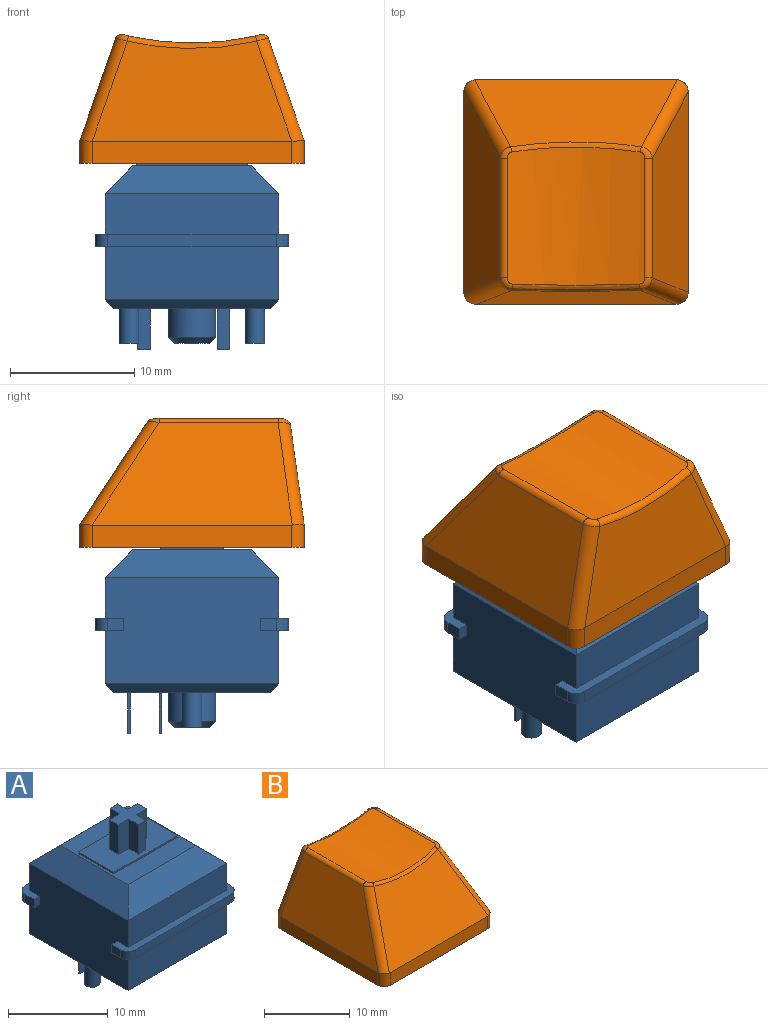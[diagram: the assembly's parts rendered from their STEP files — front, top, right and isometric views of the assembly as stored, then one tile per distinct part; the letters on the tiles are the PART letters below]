
ASSEMBLY  parts=2 mates=1
PART A: 69 faces, bbox 15.6x15.6x18.6 mm
  f0: plane 15.6x2.3mm, normal (0,0,-1), area 14.4mm2, adj f2,f3,f28,f30,f35,f60,f62,f63
  f1: plane 15.6x2.3mm, normal (0,0,-1), area 14.4mm2, adj f28,f30,f33,f34,f36,f59,f61,f64
  f2: plane 1.3x1mm, normal (1,0,0), area 1.3mm2, adj f0,f32,f62,f66
  f3: plane 1.3x1mm, normal (-1,0,0), area 1.3mm2, adj f0,f32,f63,f68
  f4: plane 15.6x2.3mm, normal (0,0,1), area 14.4mm2, adj f28,f30,f31,f33,f34,f36,f61,f64
  f5: plane 14x2.2mm, normal (-0.71,0,0.71), area 36.7mm2, adj f6,f7,f26,f30
  f6: plane 14x2.2mm, normal (0,-0.71,0.71), area 36.7mm2, adj f5,f7,f27,f31
  f7: plane 9.6x9.6mm, normal (0,0,1), area 47.2mm2, adj f5,f6,f8,f9,f10,f11,f26,f27
  f8: plane 5x0.2mm, normal (1,0,0), area 1mm2, adj f7,f9,f11,f12
  f9: plane 9x0.2mm, normal (0,1,0), area 1.8mm2, adj f7,f8,f10,f12
  f10: plane 5x0.2mm, normal (-1,0,0), area 1mm2, adj f7,f9,f11,f12
  f11: plane 9x0.2mm, normal (0,-1,0), area 1.8mm2, adj f7,f8,f10,f12
  f12: plane 9x5mm, normal (0,0,1), area 36.9mm2, adj f8,f9,f10,f11,f13,f14,f15,f16
  f13: plane 3.6x1.35mm, normal (1,0,0), area 4.9mm2, adj f12,f14,f24,f25
  f14: plane 3.6x1.08mm, normal (0,1,0), area 3.9mm2, adj f12,f13,f15,f25
  f15: plane 3.6x1.35mm, normal (-1,0,0), area 4.9mm2, adj f12,f14,f16,f25
  f16: plane 3.6x1.46mm, normal (0,1,0), area 5.3mm2, adj f12,f15,f17,f25
  f17: plane 3.6x1.3mm, normal (-1,0,0), area 4.7mm2, adj f12,f16,f18,f25
  f18: plane 3.6x1.46mm, normal (0,-1,0), area 5.3mm2, adj f12,f17,f19,f25
  f19: plane 3.6x1.35mm, normal (-1,0,0), area 4.9mm2, adj f12,f18,f20,f25
  f20: plane 3.6x1.08mm, normal (0,-1,0), area 3.9mm2, adj f12,f19,f21,f25
  f21: plane 3.6x1.35mm, normal (1,0,0), area 4.9mm2, adj f12,f20,f22,f25
  f22: plane 3.6x1.46mm, normal (0,-1,0), area 5.3mm2, adj f12,f21,f23,f25
  f23: plane 3.6x1.3mm, normal (1,0,0), area 4.7mm2, adj f12,f22,f24,f25
  f24: plane 3.6x1.46mm, normal (0,1,0), area 5.3mm2, adj f12,f13,f23,f25
  f25: plane 4x4mm, normal (0,0,1), area 8.1mm2, adj f13,f14,f15,f16,f17,f18,f19,f20
  f26: plane 14x2.2mm, normal (0,0.71,0.71), area 36.7mm2, adj f5,f7,f27,f29
  f27: plane 14x2.2mm, normal (0.71,0,0.71), area 36.7mm2, adj f6,f7,f26,f28
  f28: plane 14x8.6mm, normal (1,0,0), area 117.4mm2, adj f0,f1,f4,f27,f29,f31,f32,f55
  f29: plane 14x3.3mm, normal (0,1,0), area 46.2mm2, adj f26,f28,f30,f32
  f30: plane 14x8.6mm, normal (-1,0,0), area 117.4mm2, adj f0,f1,f4,f5,f29,f31,f32,f57
  f31: plane 14x3.3mm, normal (0,-1,0), area 46.2mm2, adj f4,f6,f28,f30
  f32: plane 15.6x2.3mm, normal (0,0,1), area 14.4mm2, adj f2,f3,f28,f29,f30,f35,f62,f63
  f33: plane 13.6x1mm, normal (0,-1,0), area 13.6mm2, adj f1,f4,f61,f64
  f34: plane 1.3x1mm, normal (1,0,0), area 1.3mm2, adj f1,f4,f61,f65
  f35: plane 13.6x1mm, normal (0,1,0), area 13.6mm2, adj f0,f32,f62,f63
  f36: plane 1.3x1mm, normal (-1,0,0), area 1.3mm2, adj f1,f4,f64,f67
  f37: plane 2.85x2.85mm, normal (0,0,-1), area 6.4mm2, adj f38
  f38: cone r=1.43mm half-angle=45deg, axis (0,0,1), area 7.4mm2, adj f37,f43
  f39: plane 1x0.2mm, normal (0,0,-1), area 0.2mm2, adj f44,f45,f46,f47
  f40: plane 1x0.2mm, normal (0,0,-1), area 0.2mm2, adj f48,f49,f50,f51
  f41: plane 1.6x1.6mm, normal (0,0,-1), area 2mm2, adj f52
  f42: plane 1.6x1.6mm, normal (0,0,-1), area 2mm2, adj f53
  f43: cylinder r=1.93mm len=3.85mm, axis (0,0,1), area 27.8mm2, adj f38,f54
  f44: plane 3.3x0.2mm, normal (-1,0,0), area 0.7mm2, adj f39,f45,f47,f54
  f45: plane 3.3x1mm, normal (0,1,0), area 3.3mm2, adj f39,f44,f46,f54
  f46: plane 3.3x0.2mm, normal (1,0,0), area 0.7mm2, adj f39,f45,f47,f54
  f47: plane 3.3x1mm, normal (0,-1,0), area 3.3mm2, adj f39,f44,f46,f54
  f48: plane 3.3x0.2mm, normal (-1,0,0), area 0.7mm2, adj f40,f49,f51,f54
  f49: plane 3.3x1mm, normal (0,1,0), area 3.3mm2, adj f40,f48,f50,f54
  f50: plane 3.3x0.2mm, normal (1,0,0), area 0.7mm2, adj f40,f49,f51,f54
  f51: plane 3.3x1mm, normal (0,-1,0), area 3.3mm2, adj f40,f48,f50,f54
  f52: cylinder r=0.8mm len=2.8mm, axis (0,0,1), area 14.1mm2, adj f41,f54
  f53: cylinder r=0.8mm len=2.8mm, axis (0,0,1), area 14.1mm2, adj f42,f54
  f54: plane 12.6x12.6mm, normal (0,0,-1), area 142.7mm2, adj f43,f44,f45,f46,f47,f48,f49,f50
  f55: plane 14x0.7mm, normal (0.71,0,-0.71), area 13.2mm2, adj f28,f54,f56,f58
  f56: plane 14x0.7mm, normal (0,0.71,-0.71), area 13.2mm2, adj f54,f55,f57,f60
  f57: plane 14x0.7mm, normal (-0.71,0,-0.71), area 13.2mm2, adj f30,f54,f56,f58
  f58: plane 14x0.7mm, normal (0,-0.71,-0.71), area 13.2mm2, adj f54,f55,f57,f59
  f59: plane 14x4.3mm, normal (0,-1,0), area 60.2mm2, adj f1,f28,f30,f58
  f60: plane 14x4.3mm, normal (0,1,0), area 60.2mm2, adj f0,f28,f30,f56
  f61: cylinder r=1mm len=1mm, axis (0,0,-1), area 1.6mm2, adj f1,f4,f33,f34
  f62: cylinder r=1mm len=1mm, axis (0,0,1), area 1.6mm2, adj f0,f2,f32,f35
  f63: cylinder r=1mm len=1mm, axis (0,0,-1), area 1.6mm2, adj f0,f3,f32,f35
  f64: cylinder r=1mm len=1mm, axis (0,0,1), area 1.6mm2, adj f1,f4,f33,f36
  f65: plane 1x0.8mm, normal (0,1,0), area 0.8mm2, adj f1,f4,f28,f34
  f66: plane 1x0.8mm, normal (0,-1,0), area 0.8mm2, adj f0,f2,f28,f32
  f67: plane 1x0.8mm, normal (0,1,0), area 0.8mm2, adj f1,f4,f30,f36
  f68: plane 1x0.8mm, normal (0,-1,0), area 0.8mm2, adj f0,f3,f30,f32
PART B: 50 faces, bbox 18.3x18.1x10.5 mm
  f0: plane 18.1x18.1mm, normal (0,0,-1), area 67.5mm2, adj f1,f2,f3,f4,f10,f12,f14,f16
  f1: plane 16.1x1.8mm, normal (1,0,0), area 29mm2, adj f0,f8,f10,f16
  f2: plane 16.1x1.8mm, normal (0,1,0), area 29mm2, adj f0,f5,f14,f15,f16,f17
  f3: plane 16.1x1.8mm, normal (-1,0,0), area 29mm2, adj f0,f6,f12,f14
  f4: plane 16.1x1.8mm, normal (0,-1,0), area 29mm2, adj f0,f7,f10,f12
  f5: plane 16.08x8.06mm, normal (0,0.99,0.14), area 103.6mm2, adj f2,f15,f17,f20
  f6: plane 16.16x8.27mm, normal (-0.94,0,0.33), area 112.8mm2, adj f3,f12,f13,f14,f15,f19
  f7: plane 16.36x8.28mm, normal (0,-0.84,0.55), area 128.1mm2, adj f4,f10,f11,f12,f13,f23
  f8: plane 16.16x8.27mm, normal (0.94,0,0.33), area 112.8mm2, adj f1,f10,f11,f16,f17,f24
  f9: cylinder r=22.9mm len=11.13mm, axis (0,-1,0), area 122.7mm2, adj f18,f19,f20,f21,f22,f23,f24,f25
  f10: cylinder r=1mm len=1.87mm, axis (0,0,-1), area 2.9mm2, adj f0,f1,f4,f7,f8,f11
  f11: cylinder r=1mm len=8.74mm, axis (0.28,-0.53,-0.8), area 14.3mm2, adj f7,f8,f10,f25
  f12: cylinder r=1mm len=1.87mm, axis (0,0,1), area 2.9mm2, adj f0,f3,f4,f6,f7,f13
  f13: cylinder r=1mm len=8.74mm, axis (0.28,0.53,0.8), area 14.3mm2, adj f6,f7,f12,f21
  f14: cylinder r=1mm len=1.83mm, axis (0,0,-1), area 2.9mm2, adj f0,f2,f3,f6,f15
  f15: cylinder r=1mm len=8.48mm, axis (-0.33,0.13,-0.94), area 13.4mm2, adj f2,f5,f6,f14,f18
  f16: cylinder r=1mm len=1.83mm, axis (0,0,1), area 2.9mm2, adj f0,f1,f2,f8,f17
  f17: cylinder r=1mm len=8.48mm, axis (-0.33,-0.13,0.94), area 13.4mm2, adj f2,f5,f8,f16,f22
  f18: bspline ~1.24x1.22mm, area 0.9mm2, adj f9,f15,f19,f20
  f19: cylinder r=0.5mm len=9.6mm, axis (0,-1,0), area 7.1mm2, adj f6,f9,f18,f21
  f20: bspline ~10.43x1.01mm, area 7.4mm2, adj f5,f9,f18,f22
  f21: bspline ~1.28x1.11mm, area 0.7mm2, adj f9,f13,f19,f23
  f22: bspline ~1.22x1.09mm, area 0.9mm2, adj f9,f17,f20,f24
  f23: bspline ~10.56x0.82mm, area 5.3mm2, adj f7,f9,f21,f25
  f24: cylinder r=0.5mm len=9.6mm, axis (0,-1,0), area 7.1mm2, adj f8,f9,f22,f25
  f25: bspline ~1.28x1.11mm, area 0.7mm2, adj f9,f11,f23,f24
  f26: plane 16.1x1.63mm, normal (-1,0,0), area 26.2mm2, adj f0,f27,f29,f32,f33
  f27: plane 16.1x1.73mm, normal (0,-1,0), area 27.9mm2, adj f0,f26,f28,f30,f31,f33
  f28: plane 16.1x1.63mm, normal (1,0,0), area 26.2mm2, adj f0,f27,f29,f31,f32
  f29: plane 16.1x1.5mm, normal (0,1,0), area 24.2mm2, adj f0,f26,f28,f32
  f30: plane 16.03x7.58mm, normal (0,-0.99,-0.14), area 97.9mm2, adj f27,f31,f33,f34
  f31: plane 16.02x7.68mm, normal (0.94,0,-0.33), area 105.7mm2, adj f27,f28,f30,f32,f34
  f32: plane 16.1x7.81mm, normal (0,0.84,-0.55), area 120.3mm2, adj f26,f28,f29,f31,f33,f34
  f33: plane 16.02x7.68mm, normal (-0.94,0,-0.33), area 105.7mm2, adj f26,f27,f30,f32,f34
  f34: cylinder r=23.9mm len=10.72mm, axis (0,-1,0), area 87.1mm2, adj f30,f31,f32,f33,f46
  f35: plane 8.71x1.35mm, normal (-1,0,0), area 11.8mm2, adj f36,f44,f45,f49
  f36: plane 8.78x1.5mm, normal (0,-1,0), area 13.1mm2, adj f35,f37,f45,f49
  f37: plane 8.78x1.3mm, normal (-1,0,0), area 11.4mm2, adj f36,f38,f45,f49
  f38: plane 8.78x1.5mm, normal (0,1,0), area 13.1mm2, adj f37,f39,f45,f49
  f39: plane 8.71x1.35mm, normal (-1,0,0), area 11.8mm2, adj f38,f40,f45,f49
  f40: plane 8.71x1mm, normal (0,1,0), area 8.7mm2, adj f39,f41,f45,f49
  f41: plane 8.71x1.35mm, normal (1,0,0), area 11.8mm2, adj f40,f42,f45,f49
  f42: plane 8.78x1.5mm, normal (0,1,0), area 13.1mm2, adj f41,f43,f45,f49
  f43: plane 8.78x1.3mm, normal (1,0,0), area 11.4mm2, adj f42,f45,f47,f49
  f44: plane 8.71x1mm, normal (0,-1,0), area 8.7mm2, adj f35,f45,f48,f49
  f45: plane 5.5x5.5mm, normal (0,0,-1), area 15.9mm2, adj f35,f36,f37,f38,f39,f40,f41,f42
  f46: cylinder r=2.75mm len=8.86mm, axis (0,0,-1), area 151.7mm2, adj f34,f45
  f47: plane 8.78x1.5mm, normal (0,-1,0), area 13.1mm2, adj f43,f45,f48,f49
  f48: plane 8.71x1.35mm, normal (1,0,0), area 11.8mm2, adj f44,f45,f47,f49
  f49: cylinder r=23.9mm len=4mm, axis (0,-1,0), area 7.9mm2, adj f35,f36,f37,f38,f39,f40,f41,f42
PLACE A at identity fixed
PLACE B rot(axis=(0,0,1),180deg) t=(0,0,11.7)mm
MATE fastened B.f46 <-> A.f38  axis (0,0,-1) through (0,0,11.7)mm
